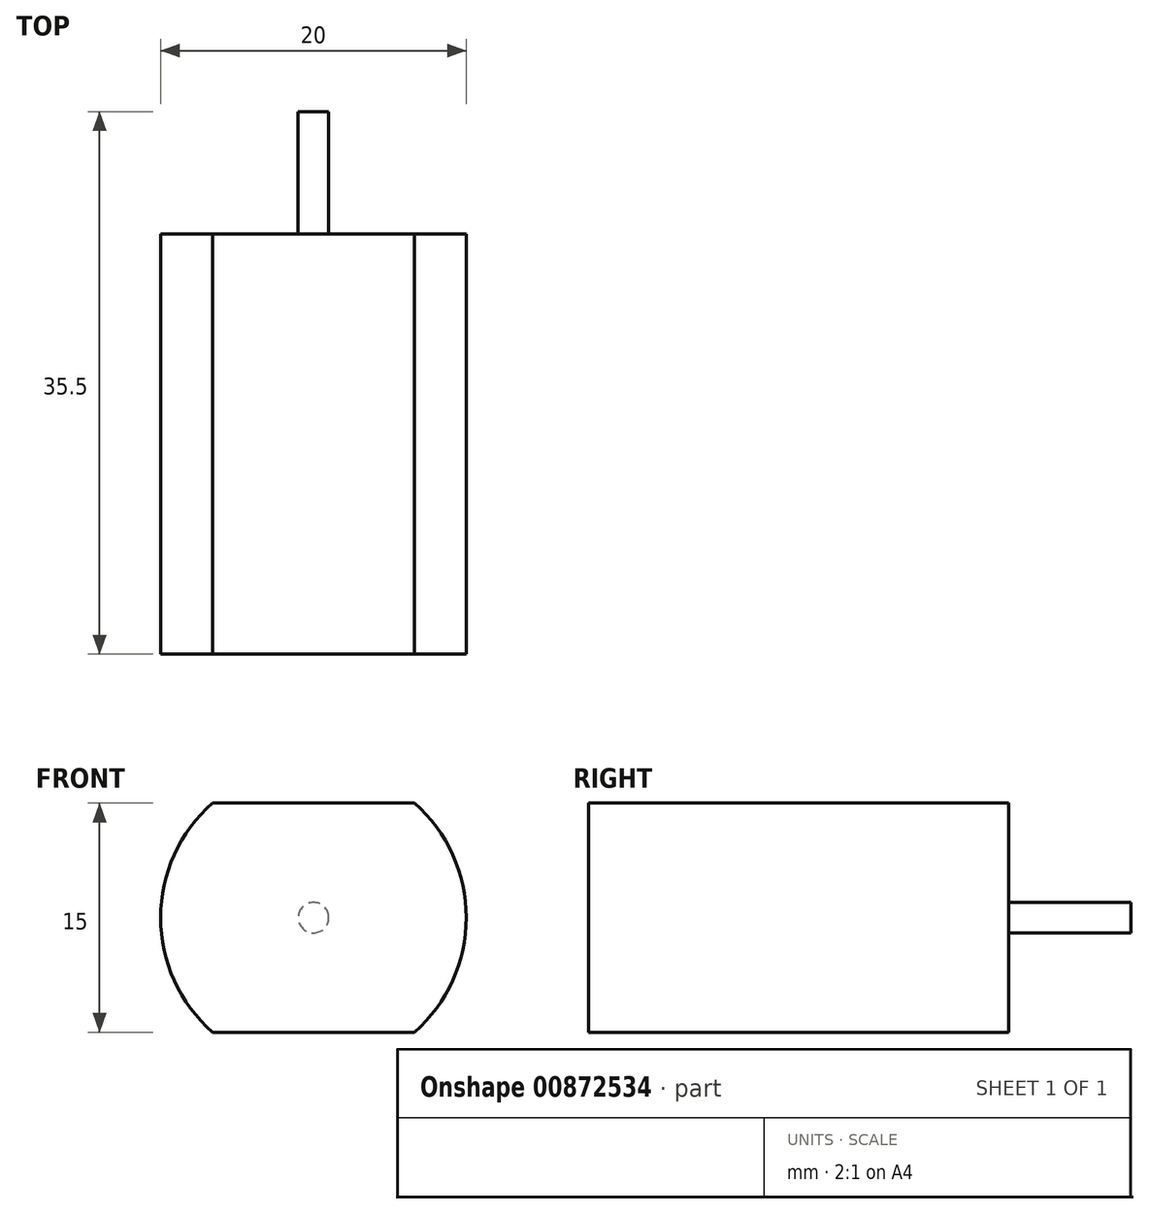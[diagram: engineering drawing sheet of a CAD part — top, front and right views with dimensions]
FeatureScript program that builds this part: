
annotation { "Feature Type Name" : "Feature", "Feature Type Description" : "" }
export const myFeature = defineFeature(function(context is Context, id is Id, definition is map)
    precondition{}
    {
        {
            var Q0;
            Q0=qCreatedBy(makeId("Front.planeOp"),FACE);
            var sketch = newSketch(context, id + "F0", { "sketchPlane" : qUnion([Q0])});
            skArc(sketch, "E0", {"start": v(-6.61, 7.5) * mm, "mid": v(-10, 0) * mm, "end": v(-6.61, -7.5) * mm});
            skLineSegment(sketch, "E1.bottom", {"start": v(-6.61, 7.5) * mm, "end": v(6.61, 7.5) * mm});
            skLineSegment(sketch, "E1.top", {"start": v(-6.61, -7.5) * mm, "end": v(6.61, -7.5) * mm});
            skLineSegment(sketch, "E1.left", {"start": v(-6.61, 7.5) * mm, "end": v(-6.61, -7.5) * mm});
            skLineSegment(sketch, "E1.right", {"start": v(6.61, 7.5) * mm, "end": v(6.61, -7.5) * mm});
            skArc(sketch, "E2.trimOffspring", {"start": v(6.61, -7.5) * mm, "mid": v(10, 0) * mm, "end": v(6.61, 7.5) * mm});
            skSolve(sketch);
        }
        {
            var Q0;
            Q0 = qSketchRegion(id + "F0", true);
            extrude(context, id + "F1", {"entities" : qUnion([Q0]), "depth" : 27.5 * mm, "offsetDistance" : 25 * mm});
        }
        {
            var Q0;
            Q0=makeQuery(id+"F1.opExtrude","CAP_FACE",FACE,{"disambiguationData":[OSD([sQuery(id+"F0.wireOp",EDGE,"E0"),sQuery(id+"F0.wireOp",EDGE,"E1.bottom"),sQuery(id+"F0.wireOp",EDGE,"E1.top"),sQuery(id+"F0.wireOp",EDGE,"E2.trimOffspring")])],"isStart":true});
            var sketch = newSketch(context, id + "F2", { "sketchPlane" : qUnion([Q0])});
            skCircle(sketch, "E3", {"center": v(0, 0) * mm, "radius": 1 * mm});
            skSolve(sketch);
        }
        {
            var Q0;
            Q0=makeQuery(id+"F2.imprint","IMPRINT",FACE,{"disambiguationData":[TD([[makeQuery(id+"F2.imprint","IMPRINT",EDGE,{"derivedFrom":sQuery(id+"F2.wireOp",EDGE,"E3")}),1.0]])]});
            extrude(context, id + "F3", {"entities" : qUnion([Q0]), "operationType" : NewBodyOperationType.ADD, "depth" : 8 * mm, "offsetDistance" : 25 * mm});
        }
    });
